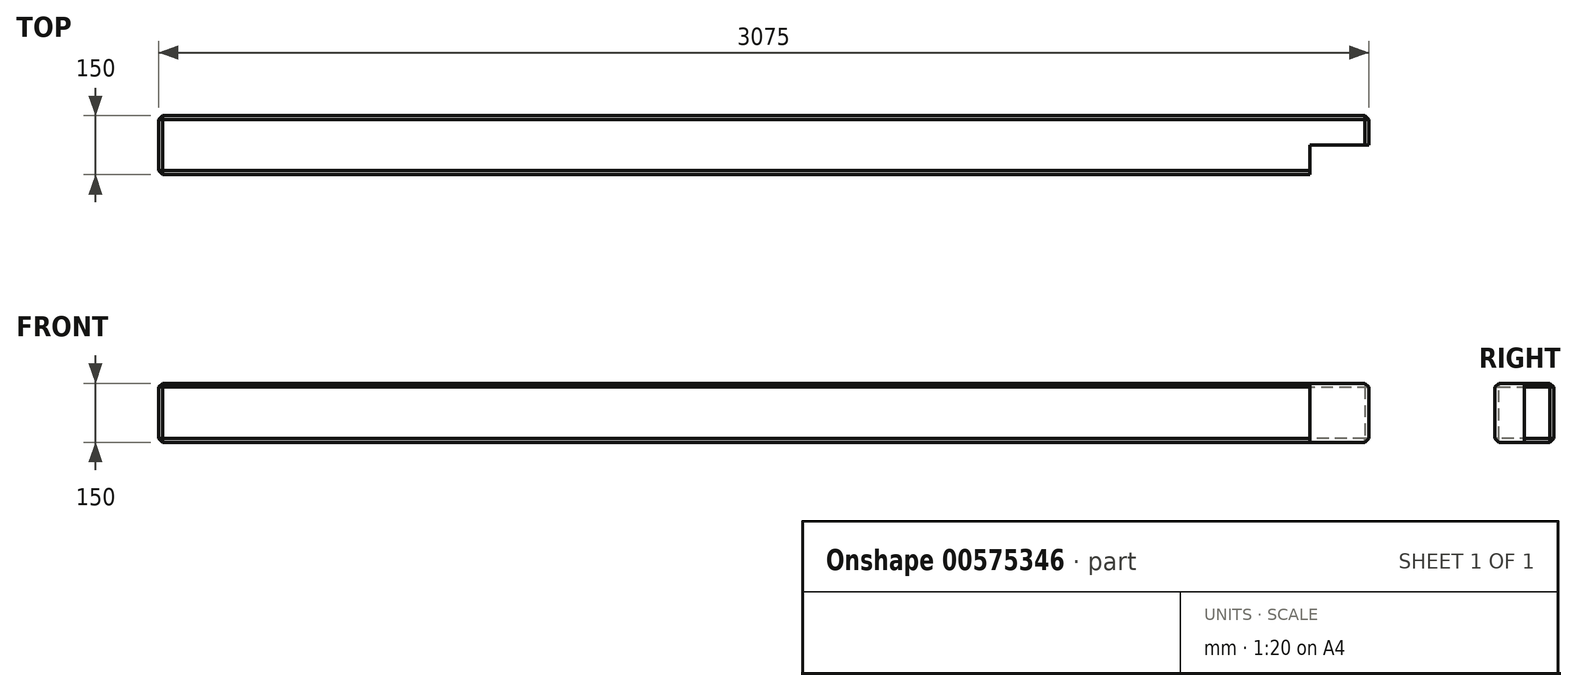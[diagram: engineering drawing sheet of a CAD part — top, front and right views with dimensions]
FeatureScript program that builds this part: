
annotation { "Feature Type Name" : "Feature", "Feature Type Description" : "" }
export const myFeature = defineFeature(function(context is Context, id is Id, definition is map)
    precondition{}
    {
        {
            var Q0;
            Q0=qCreatedBy(makeId("Top.planeOp"),FACE);
            var sketch = newSketch(context, id + "F0", { "sketchPlane" : qUnion([Q0])});
            skLineSegment(sketch, "E0.bottom", {"start": v(-1537.5, 75) * mm, "end": v(1537.5, 75) * mm});
            skLineSegment(sketch, "E0.top", {"start": v(-1537.5, -75) * mm, "end": v(1537.5, -75) * mm});
            skLineSegment(sketch, "E0.left", {"start": v(-1537.5, 75) * mm, "end": v(-1537.5, -75) * mm});
            skLineSegment(sketch, "E0.right", {"start": v(1537.5, 75) * mm, "end": v(1537.5, -75) * mm});
            skPoint(sketch, "E0.middle", {"position": v(0, 0) * mm});
            skSolve(sketch);
        }
        {
            var Q0;
            Q0=makeQuery(id+"F0.imprint","IMPRINT",FACE,{"disambiguationData":[TD([[makeQuery(id+"F0.imprint","IMPRINT",EDGE,{"derivedFrom":sQuery(id+"F0.wireOp",EDGE,"E0.bottom")}),-1.0]])]});
            extrude(context, id + "F1", {"entities" : qUnion([Q0]), "depth" : 150 * mm});
        }
        {
            var Q0;
            Q0=makeQuery(id+"F1.opExtrude","SWEPT_FACE",FACE,{"disambiguationData":[OSD([sQuery(id+"F0.wireOp",EDGE,"E0.top")])]});
            var Q1;
            Q1=makeQuery(id+"F1.opExtrude","CAP_FACE",FACE,{"disambiguationData":[OSD([sQuery(id+"F0.wireOp",EDGE,"E0.bottom"),sQuery(id+"F0.wireOp",EDGE,"E0.top"),sQuery(id+"F0.wireOp",EDGE,"E0.left"),sQuery(id+"F0.wireOp",EDGE,"E0.right")])],"isStart":false});
            var Q2;
            Q2=makeQuery(id+"F1.opExtrude","CAP_FACE",FACE,{"disambiguationData":[OSD([sQuery(id+"F0.wireOp",EDGE,"E0.bottom"),sQuery(id+"F0.wireOp",EDGE,"E0.top"),sQuery(id+"F0.wireOp",EDGE,"E0.left"),sQuery(id+"F0.wireOp",EDGE,"E0.right")])],"isStart":true});
            var Q3;
            Q3=makeQuery(id+"F1.opExtrude","SWEPT_FACE",FACE,{"disambiguationData":[OSD([sQuery(id+"F0.wireOp",EDGE,"E0.bottom")])]});
            chamfer(context, id + "F2", {"entities" : qUnion([Q0, Q1, Q2, Q3]), "width" : 10 * mm, "tangentPropagation" : true});
        }
        {
            var Q0;
            Q0=makeQuery(id+"F1.opExtrude","CAP_FACE",FACE,{"disambiguationData":[OSD([sQuery(id+"F0.wireOp",EDGE,"E0.bottom"),sQuery(id+"F0.wireOp",EDGE,"E0.top"),sQuery(id+"F0.wireOp",EDGE,"E0.left"),sQuery(id+"F0.wireOp",EDGE,"E0.right")])],"isStart":false});
            var sketch = newSketch(context, id + "F3", { "sketchPlane" : qUnion([Q0])});
            skPoint(sketch, "E1", {"position": v(1387.5, 0) * mm});
            skLineSegment(sketch, "E2.bottom", {"start": v(1387.5, 0) * mm, "end": v(1537.5, 0) * mm});
            skLineSegment(sketch, "E2.top", {"start": v(1387.5, -79.8) * mm, "end": v(1537.5, -79.8) * mm});
            skLineSegment(sketch, "E2.left", {"start": v(1387.5, 0) * mm, "end": v(1387.5, -79.8) * mm});
            skLineSegment(sketch, "E2.right", {"start": v(1537.5, 0) * mm, "end": v(1537.5, -79.8) * mm});
            skSolve(sketch);
        }
        {
            var Q0;
            {var subQ1=sQuery(id+"F3.wireOp",EDGE,"E2.top");Q0=makeQuery(id+"F3.imprint","IMPRINT",FACE,{"disambiguationData":[TD([[makeQuery(id+"F3.imprint","IMPRINT",EDGE,{"derivedFrom":subQ1}),1.0]])]});}
            var Q1;
            {var subQ0=sQuery(id+"F3.wireOp",EDGE,"E2.left");var subQ1=sQuery(id+"F3.wireOp",EDGE,"E2.bottom");var subQ2=makeQuery(id+"F3.imprint","INTERSECT",VERTEX,{"derivedFrom":[subQ1,subQ0]});Q1=makeQuery(id+"F3.imprint","IMPRINT",FACE,{"disambiguationData":[TD([[makeQuery(id+"F3.imprint","IMPRINT",EDGE,{"disambiguationData":[TD([[subQ2,-1.0]])],"derivedFrom":subQ1}),-1.0]])]});}
            extrude(context, id + "F4", {"entities" : qUnion([Q0, Q1]), "operationType" : NewBodyOperationType.REMOVE, "endBound" : BoundingType.THROUGH_ALL, "oppositeDirection" : true, "depth" : 25 * mm});
        }
    });
